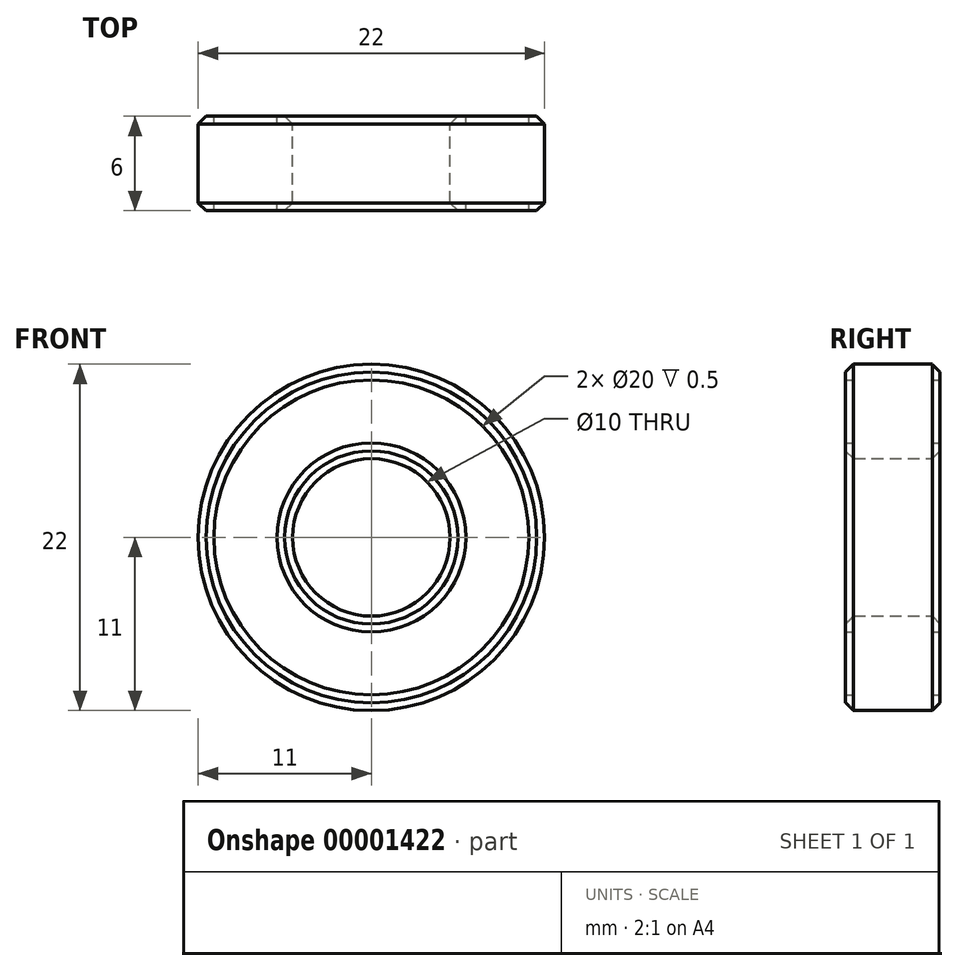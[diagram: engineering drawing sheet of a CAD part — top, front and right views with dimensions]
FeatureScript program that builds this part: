
annotation { "Feature Type Name" : "Feature", "Feature Type Description" : "" }
export const myFeature = defineFeature(function(context is Context, id is Id, definition is map)
    precondition{}
    {
        {
            var Q0;
            Q0=qCreatedBy(makeId("Right.planeOp"),FACE);
            var sketch = newSketch(context, id + "F0", { "sketchPlane" : qUnion([Q0])});
            skLineSegment(sketch, "E0", {"start": v(-3, 5) * mm, "end": v(3, 5) * mm});
            skLineSegment(sketch, "E1", {"start": v(3, 5) * mm, "end": v(3, 6) * mm});
            skLineSegment(sketch, "E2", {"start": v(3, 6) * mm, "end": v(2.5, 6) * mm});
            skLineSegment(sketch, "E3", {"start": v(2.5, 6) * mm, "end": v(2.5, 10) * mm});
            skLineSegment(sketch, "E4", {"start": v(2.5, 10) * mm, "end": v(3, 10) * mm});
            skLineSegment(sketch, "E5", {"start": v(3, 10) * mm, "end": v(3, 11) * mm});
            skLineSegment(sketch, "E6", {"start": v(3, 11) * mm, "end": v(-3, 11) * mm});
            skLineSegment(sketch, "E7", {"start": v(-3, 11) * mm, "end": v(-3, 10) * mm});
            skLineSegment(sketch, "E8", {"start": v(-3, 10) * mm, "end": v(-2.5, 10) * mm});
            skLineSegment(sketch, "E9", {"start": v(-2.5, 10) * mm, "end": v(-2.5, 6) * mm});
            skLineSegment(sketch, "E10", {"start": v(-2.5, 6) * mm, "end": v(-3, 6) * mm});
            skLineSegment(sketch, "E11", {"start": v(-3, 6) * mm, "end": v(-3, 5) * mm});
            skLineSegment(sketch, "E12", {"start": v(0, 0) * mm, "end": v(0, 5) * mm, "construction": true});
            skLineSegment(sketch, "E13", {"start": v(0, 0) * mm, "end": v(-5.67, 0) * mm, "construction": true});
            skSolve(sketch);
        }
        {
            var Q0;
            Q0=makeQuery(id+"F0.imprint","IMPRINT",FACE,{"disambiguationData":[TD([[makeQuery(id+"F0.imprint","IMPRINT",EDGE,{"derivedFrom":sQuery(id+"F0.wireOp",EDGE,"E0")}),1.0]])]});
            var Q1;
            Q1=sQuery(id+"F0.wireOp",EDGE,"E13");
            revolve(context, id + "F1", {"entities" : qUnion([Q0]), "axis" : qUnion([Q1]), "revolveType" : RevolveType.FULL});
        }
        {
            var Q0;
            Q0=makeQuery(id+"F1.opRevolve","SWEPT_EDGE",EDGE,{"disambiguationData":[OSD([sQuery(id+"F0.wireOp",EDGE,"E6"),sQuery(id+"F0.wireOp",EDGE,"E7")])]});
            var Q1;
            Q1=makeQuery(id+"F1.opRevolve","SWEPT_EDGE",EDGE,{"disambiguationData":[OSD([sQuery(id+"F0.wireOp",EDGE,"E5"),sQuery(id+"F0.wireOp",EDGE,"E6")])]});
            var Q2;
            Q2=makeQuery(id+"F1.opRevolve","SWEPT_EDGE",EDGE,{"disambiguationData":[OSD([sQuery(id+"F0.wireOp",EDGE,"E0"),sQuery(id+"F0.wireOp",EDGE,"E1")])]});
            var Q3;
            Q3=makeQuery(id+"F1.opRevolve","SWEPT_EDGE",EDGE,{"disambiguationData":[OSD([sQuery(id+"F0.wireOp",EDGE,"E0"),sQuery(id+"F0.wireOp",EDGE,"E11")])]});
            chamfer(context, id + "F2", {"entities" : qUnion([Q0, Q1, Q2, Q3]), "width" : 0.5 * mm, "tangentPropagation" : true});
        }
    });
